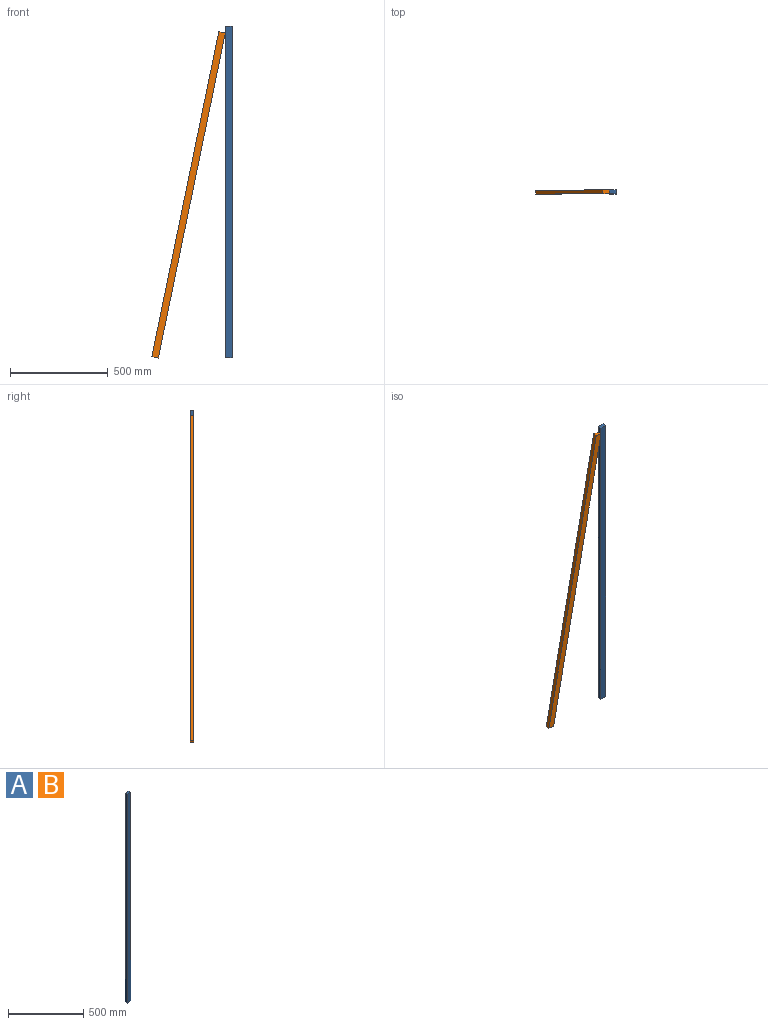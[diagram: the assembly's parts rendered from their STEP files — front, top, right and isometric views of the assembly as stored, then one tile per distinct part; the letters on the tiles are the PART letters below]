
ASSEMBLY  parts=2 mates=1
PART A: 6 faces, bbox 34.5x19.2x1700 mm
  f0: plane 1700x34.5mm, normal (0,-1,0), area 58650mm2, adj f1,f3,f4,f5
  f1: plane 1700x19.2mm, normal (1,0,0), area 32640mm2, adj f0,f2,f4,f5
  f2: plane 1700x34.5mm, normal (0,1,0), area 58650mm2, adj f1,f3,f4,f5
  f3: plane 1700x19.2mm, normal (-1,0,0), area 32640mm2, adj f0,f2,f4,f5
  f4: plane 34.5x19.2mm, normal (0,0,1), area 662.4mm2, adj f0,f1,f2,f3
  f5: plane 34.5x19.2mm, normal (0,0,-1), area 662.4mm2, adj f0,f1,f2,f3
PART B: same geometry as A
PLACE A t=(-2.74,26.88,-22.19)mm
PLACE B rot(axis=(0,1,0),11.6deg) t=(-380.13,26.88,-19.35)mm
MATE planar A.f0 <-> B.f0  axis (0,-1,0) through (-19.99,17.28,-22.19)mm
